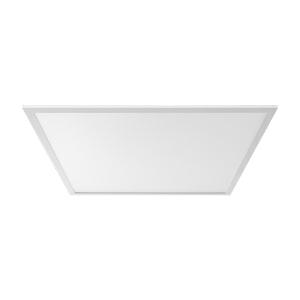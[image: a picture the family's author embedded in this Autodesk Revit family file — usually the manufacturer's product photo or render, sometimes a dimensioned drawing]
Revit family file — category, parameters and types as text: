
# Revit family: 3f_filippi_-_3f_led_panel_3f_filippi_-_22791_a01486_-_3flp6060ugr-840__1100ma____dali_0c68
name_source: partatom
category: Lighting Fixtures
units: mm (PartAtom-declared; Revit-internal decimal feet)

## family parameters
Cut with Voids When Loaded = No
Host = Face
Light Source = No
Part Type = Normal
Room Calculation Point = No
Round Connector Dimension = Use Diameter
Shared = No

## types (1)
- 3F Filippi - 3F LED Panel (1 x LED, 5272 lm, 43 W, 4000 K)
    Apparent Load = 43 VA
    Approval mark = ENEC
    CIE Flux Codes = 63 89 97 100 100
    Color Rendering = 80
    Color Temperature = 4000 K
    Control Gear = Electronic transformer
    Default Elevation = 1800 mm
    Description = ILLUMINOTECHNICAL
Luminous efficiency 100% (DLOR 100%, ULOR 0%).
Initial luminous flux of the luminaire 5272 lm.
Direct symmetric distribution.
Installation Interdistance Transv.D = 1.18 x hu - Long.D = 1.30 x hu.
Average luminance <3000 cd/m² for radial angles >65°.
Tabular UGR (CIE 117 - 4H-8H; S=0.25H; 70/50/20): RUG 19.1 - 19.3.
Beam angle: 86° - 90°.
Luminous efficacy 123 lm/W.
Lifetime (L93/B10): 30000 h. (tq+25°C)
Lifetime (L90/B10): 50000 h. (tq+25°C)
Lifetime (L80/B10): 80000 h. (tq+25°C)
Lifetime (L75/B10): 100000 h. (tq+25°C)
Sudden decreased luminous flux after 50000 hours: 0% (C0).
Photobiological safety in compliance with IEC/TR 62778: RG0 risk exempt, (IEC 62471).
In compliance with IEC/EN 62722-2-1 - IEC/EN 62717 standards.

SOURCE
2 linear LED modules 840.
Energy efficiency class (UE 2019/2020 - UE 2019/2015): B.
CIE 13.3 Colour rendering index: CRI >80 (R9 <50%).
IES TM-30 Fidelity Index: Rf = 83 Rg = 94.
CCT nominal colour temperature 4000 K.
Colour initial tolerance (MacAdam): SDCM 3.

MECHANICAL
Housing in white painted epoxy-polyester powder aluminium.
Diffuser in SMP trasparent microprismatic methacrylate (PMMA) externally, anti-glare with high transmittance.
Perimetral frame in white polycarbonate.
Anti-fall safety cable.
Luminaire with limited surface temperature. - D - (EN 60598-2-24)
Dimensions: 595x595 mm, height 9 mm. Weight 2.71 kg.
IP43 protection degree for exposed part, IP20 for recessed part.
Mechanical strength to impacts IK06 (1 joule).
Glow-wire test resistance 650°C.

ELECTRICAL
Wiring on a separate unit (Multi-current power supply, to be ordered separately).
Power of the luminaire 43 W.
CE - IEC 60598-1 - EN 60598-1.
SAFE FLICKER: PstLM=<1 and SVM=<0.4 (IEC TR 61547-1 and IEC TR 63158), to ensure a more comfortable and safe light.
Luminaire compliant with EN 60598-2-22 for power supply from a centralised emergency system CPSS (Central Power Supply System), not incorporated in the luminaire - high risk areas excluded. The default power and flux are 100% in AC and 100% in DC.
Ambient temperature from 0°C to +25°C.
Temperature class T6 max 85°C.
Relative humidity UR: <85%.

INSTALLATION
Lay-in recessed fitting / Pull-up recessed fitting with brackets / Ceiling installation with frame / Suspension via accessory.
All accessories dedicated to this product are available on the Catalog and on our website www.3F-Filippi.com.

ACCESSORIES
A01486 - DELT40C-MEL DRIVER DALI DIP-SWITCH.
DALI, PUSH-DIM, electronic wiring 230V-50/60Hz, power factor 0.95 at full load, constant output current, SELV, class II, 1 driver, 1 DALI addresse.
Multi-current power supply that allows you to choose the driving current of the fixture at the time of installation (default 900mA) according to the required illuminance.
Quick connection non-reversible plug-socket terminal block, also for cascade connection.

APPLICATIONS
Suitable product for food production plants (HACCP), IFS (Food Version 6), BRC (GSFS Food Version 7).
Environments: with VDTs, meeting rooms, offices.
Environments: recreational, transit areas, corridors, schools, stairwells.
Environments where soft diffuse light is required for optimal visual comfort.

WARNING
Luminaire designed for disposal/recycling at end-of-life.
Replaceable control gear by a professional.
    Height = 0 mm  [stored 0 ft]
    Lamp = 1 x LED
    Lamp Light Flux = 5272 lm
    Lamp Power = 43 W
    Lamp count = 1
    Length = 595 mm
    Lifetime = 50000 h
    Luminous efficacy = 123 lm/W
    Manufacturer = 3F Filippi
    ModVariant = No
    Model = 3F Filippi - 22791+A01486 - 3FLP6060UGR-840 (1100mA) + DALI
    Mounting Place = Ceiling
    Mounting Type = Recessed
    Number of Poles = 1
    OnlyDefault = Yes
    Power Factor = 1
    Product Name = 3F Filippi - 3F LED Panel
    Product group = recessed luminaire
    ProductGroupID = 4
    Protection Class = Protection class II
    Protection Degree = IP 20
    RLX_Detail_Level = 1
    RLX_Emergency_Light_Flux = 0 lm
    RLX_Emergency_Type = 0
    RLX_Emergency_Type_DB = No
    RlxData = <blob elided: 32089 chars, md5=56d07f09>
    Socket = socket
    Standby Power = 0 W
    System Light Flux = 5272 lm
    System Power = 43 W
    Type Comments = Product without accessories
    Type Image = 3ffilippi_3f_led_panel_596x596.jpg
    URL = http://relux.com
    VarID = ---
    Voltage = 0 V
    Weight = 0.00 kg
    Width = 595 mm

note: [stored X ft] marks values corroborated as IEEE doubles in the binary element streams (Revit-internal decimal feet)

## geometry (parser evidence)
native form markers: Blend x4, Sweep x11
no freeform markers — native parametric forms only
